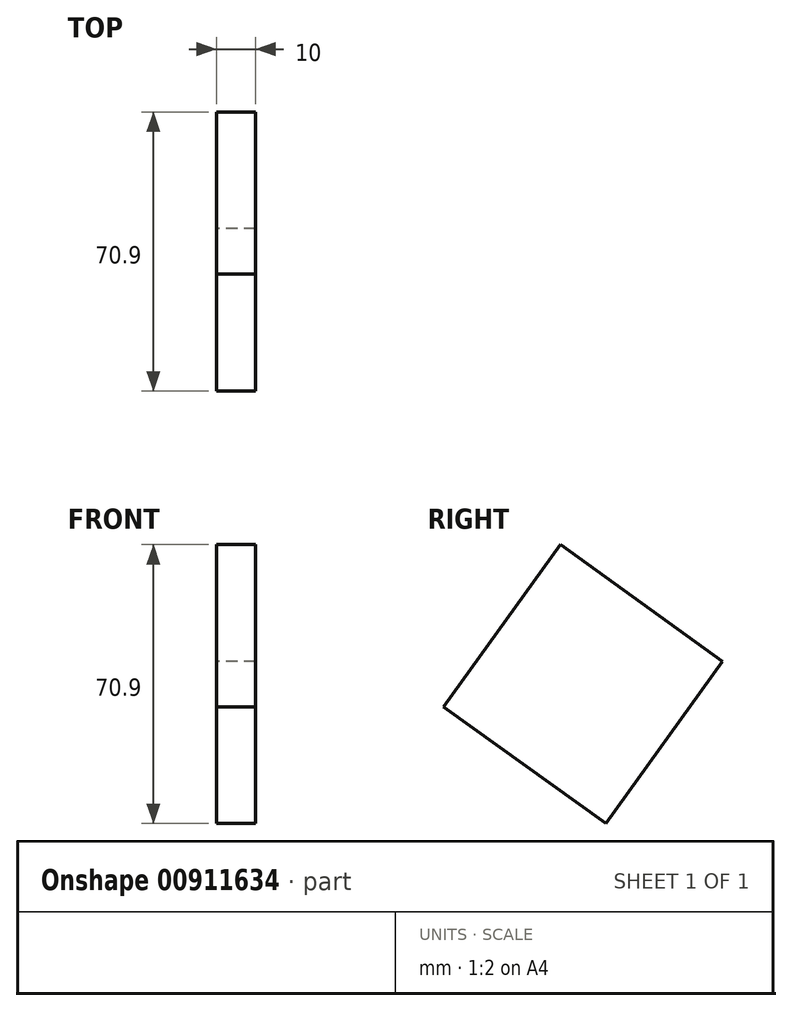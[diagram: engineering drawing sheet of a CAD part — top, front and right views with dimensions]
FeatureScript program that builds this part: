
annotation { "Feature Type Name" : "Feature", "Feature Type Description" : "" }
export const myFeature = defineFeature(function(context is Context, id is Id, definition is map)
    precondition{}
    {
        {
            var Q0;
            Q0=qCreatedBy(makeId("Right.planeOp"),FACE);
            var sketch = newSketch(context, id + "F0", { "sketchPlane" : qUnion([Q0])});
            skLineSegment(sketch, "E0", {"start": v(-70.06, 25.42) * mm, "end": v(-99.73, -15.82) * mm});
            skLineSegment(sketch, "E1", {"start": v(-99.73, -15.82) * mm, "end": v(-58.5, -45.48) * mm});
            skLineSegment(sketch, "E2", {"start": v(-58.5, -45.48) * mm, "end": v(-28.83, -4.25) * mm});
            skLineSegment(sketch, "E3", {"start": v(-28.83, -4.25) * mm, "end": v(-70.06, 25.42) * mm});
            skSolve(sketch);
        }
        {
            var Q0;
            Q0=makeQuery(id+"F0.imprint","IMPRINT",FACE,{"disambiguationData":[TD([[makeQuery(id+"F0.imprint","IMPRINT",EDGE,{"derivedFrom":sQuery(id+"F0.wireOp",EDGE,"E0")}),1.0]])]});
            extrude(context, id + "F1", {"entities" : qUnion([Q0]), "depth" : 10 * mm, "offsetDistance" : 25.4 * mm});
        }
    });
